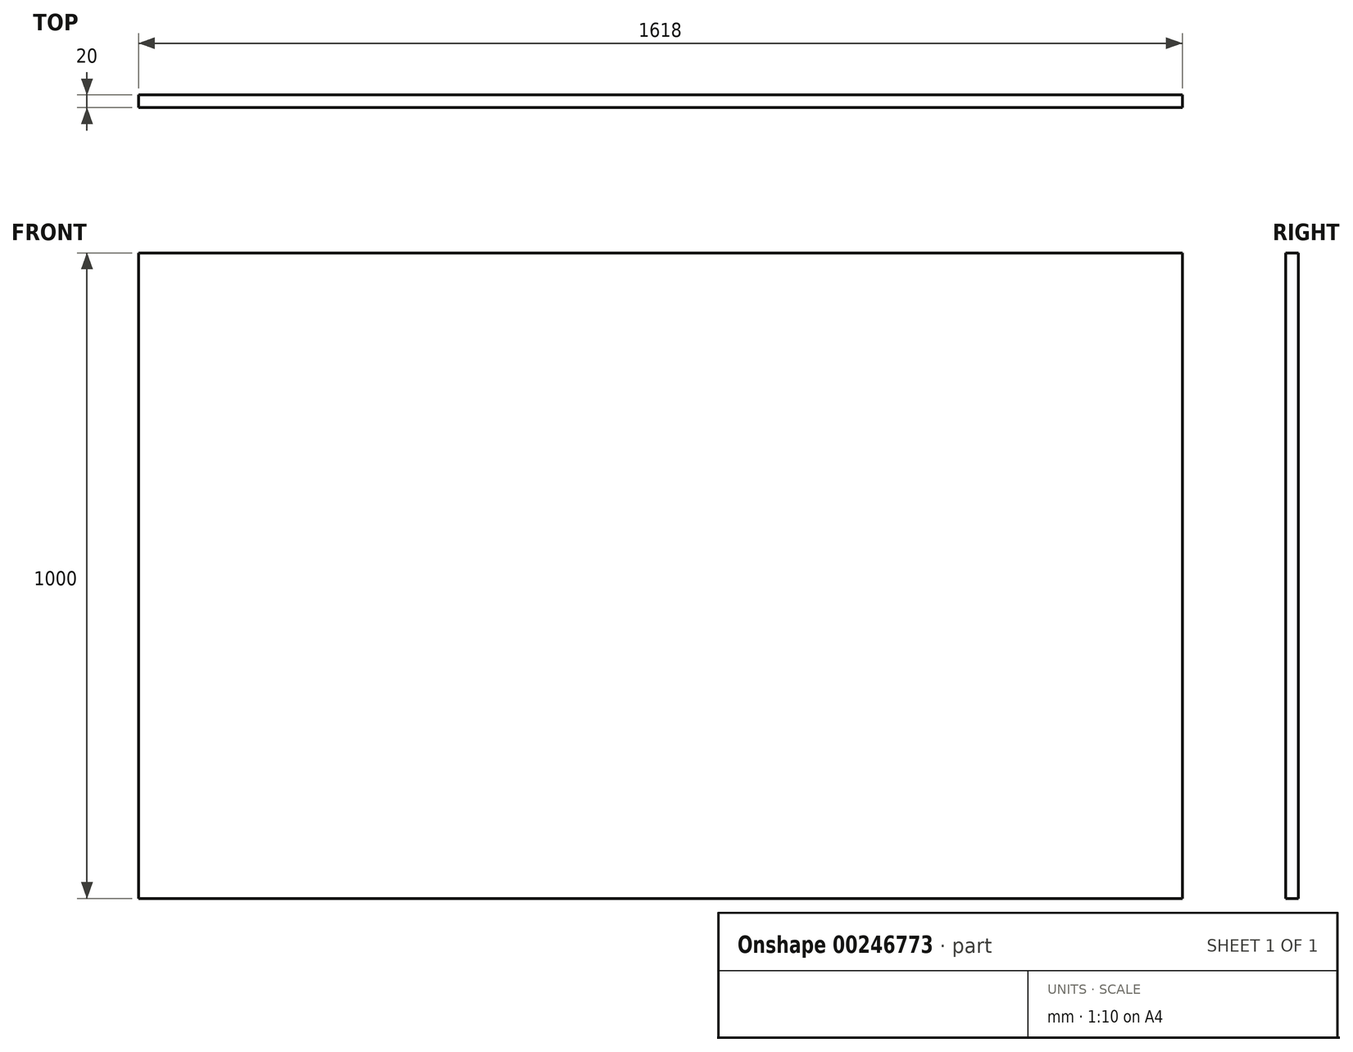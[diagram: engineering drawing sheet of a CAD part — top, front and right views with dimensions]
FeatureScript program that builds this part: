
annotation { "Feature Type Name" : "Feature", "Feature Type Description" : "" }
export const myFeature = defineFeature(function(context is Context, id is Id, definition is map)
    precondition{}
    {
        {
            var Q0;
            Q0=qCreatedBy(makeId("Front.planeOp"),FACE);
            var sketch = newSketch(context, id + "F0", { "sketchPlane" : qUnion([Q0])});
            skLineSegment(sketch, "E0.bottom", {"start": v(-860.66, 609.67) * mm, "end": v(757.34, 609.67) * mm});
            skLineSegment(sketch, "E0.top", {"start": v(-860.66, -390.33) * mm, "end": v(757.34, -390.33) * mm});
            skLineSegment(sketch, "E0.left", {"start": v(-860.66, 609.67) * mm, "end": v(-860.66, -390.33) * mm});
            skLineSegment(sketch, "E0.right", {"start": v(757.34, 609.67) * mm, "end": v(757.34, -390.33) * mm});
            skSolve(sketch);
        }
        {
            var Q0;
            Q0=makeQuery(id+"F0.imprint","IMPRINT",FACE,{"disambiguationData":[TD([[makeQuery(id+"F0.imprint","IMPRINT",EDGE,{"derivedFrom":sQuery(id+"F0.wireOp",EDGE,"E0.bottom")}),-1.0]])]});
            extrude(context, id + "F1", {"entities" : qUnion([Q0]), "depth" : 20 * mm});
        }
    });
